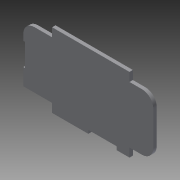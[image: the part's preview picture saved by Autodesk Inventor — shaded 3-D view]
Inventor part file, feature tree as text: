
AUTODESK INVENTOR PART (.ipt)
format: ipt  version: 2015 (Build 190159000, 159)  size: 110,080 bytes
history: native  units: mm
features: extrude x1, fillet x1, sketch x1
ambient origin geometry x8: Origin, YZ Plane, XZ Plane, XY Plane, X Axis, Y Axis, Z Axis, Center Point
bodies: Solid1 (feature_tree)
feature tree (3):
  extrude  "Extrusion1"  Depth=42.2mm
  fillet  "Fillet1"  Radius=15.4mm
  sketch  "Sketch1"  dims[d0=230.0mm d2=42.2mm d3=15.4mm d4=42.2mm d5=15.4mm d13=31.0mm d16=6.0mm d17=0.0mm d18=20.0mm d21=6.0mm d26=3.0mm d27=51.0mm d28=51.0mm]
